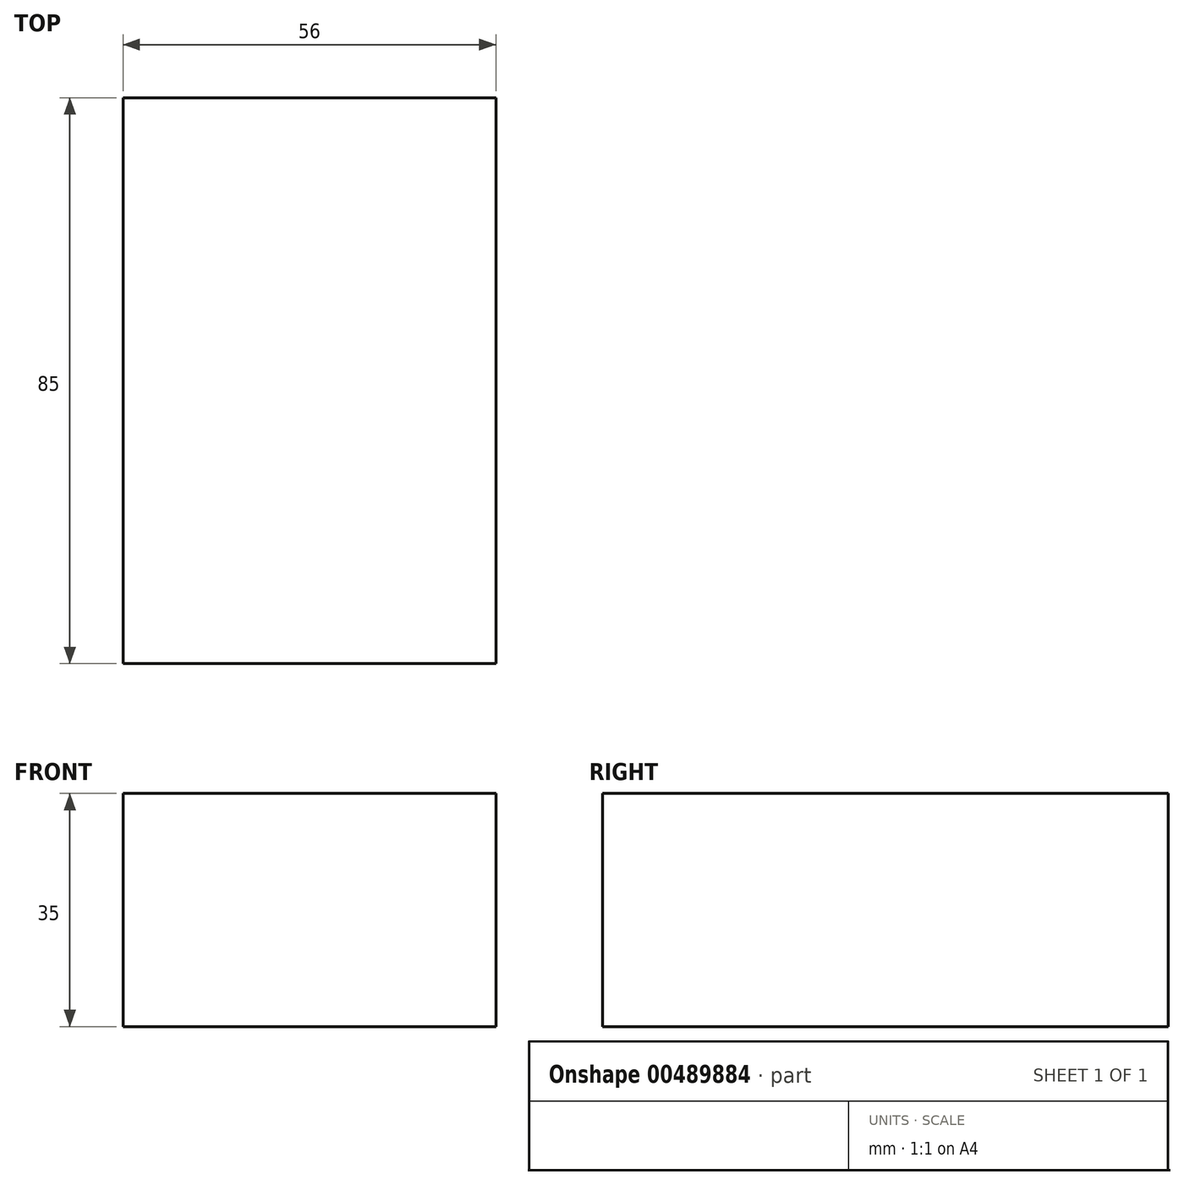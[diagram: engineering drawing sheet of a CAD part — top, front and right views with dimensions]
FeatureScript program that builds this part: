
annotation { "Feature Type Name" : "Feature", "Feature Type Description" : "" }
export const myFeature = defineFeature(function(context is Context, id is Id, definition is map)
    precondition{}
    {
        {
            var Q0;
            Q0=qCreatedBy(makeId("Top.planeOp"),FACE);
            var sketch = newSketch(context, id + "F0", { "sketchPlane" : qUnion([Q0])});
            skLineSegment(sketch, "E0.bottom", {"start": v(28, -42.5) * mm, "end": v(-28, -42.5) * mm});
            skLineSegment(sketch, "E0.top", {"start": v(28, 42.5) * mm, "end": v(-28, 42.5) * mm});
            skLineSegment(sketch, "E0.left", {"start": v(28, -42.5) * mm, "end": v(28, 42.5) * mm});
            skLineSegment(sketch, "E0.right", {"start": v(-28, -42.5) * mm, "end": v(-28, 42.5) * mm});
            skPoint(sketch, "E0.middle", {"position": v(0, 0) * mm});
            skSolve(sketch);
        }
        {
            var Q0;
            Q0 = qSketchRegion(id + "F0", true);
            extrude(context, id + "F1", {"entities" : qUnion([Q0]), "depth" : 35 * mm});
        }
    });
